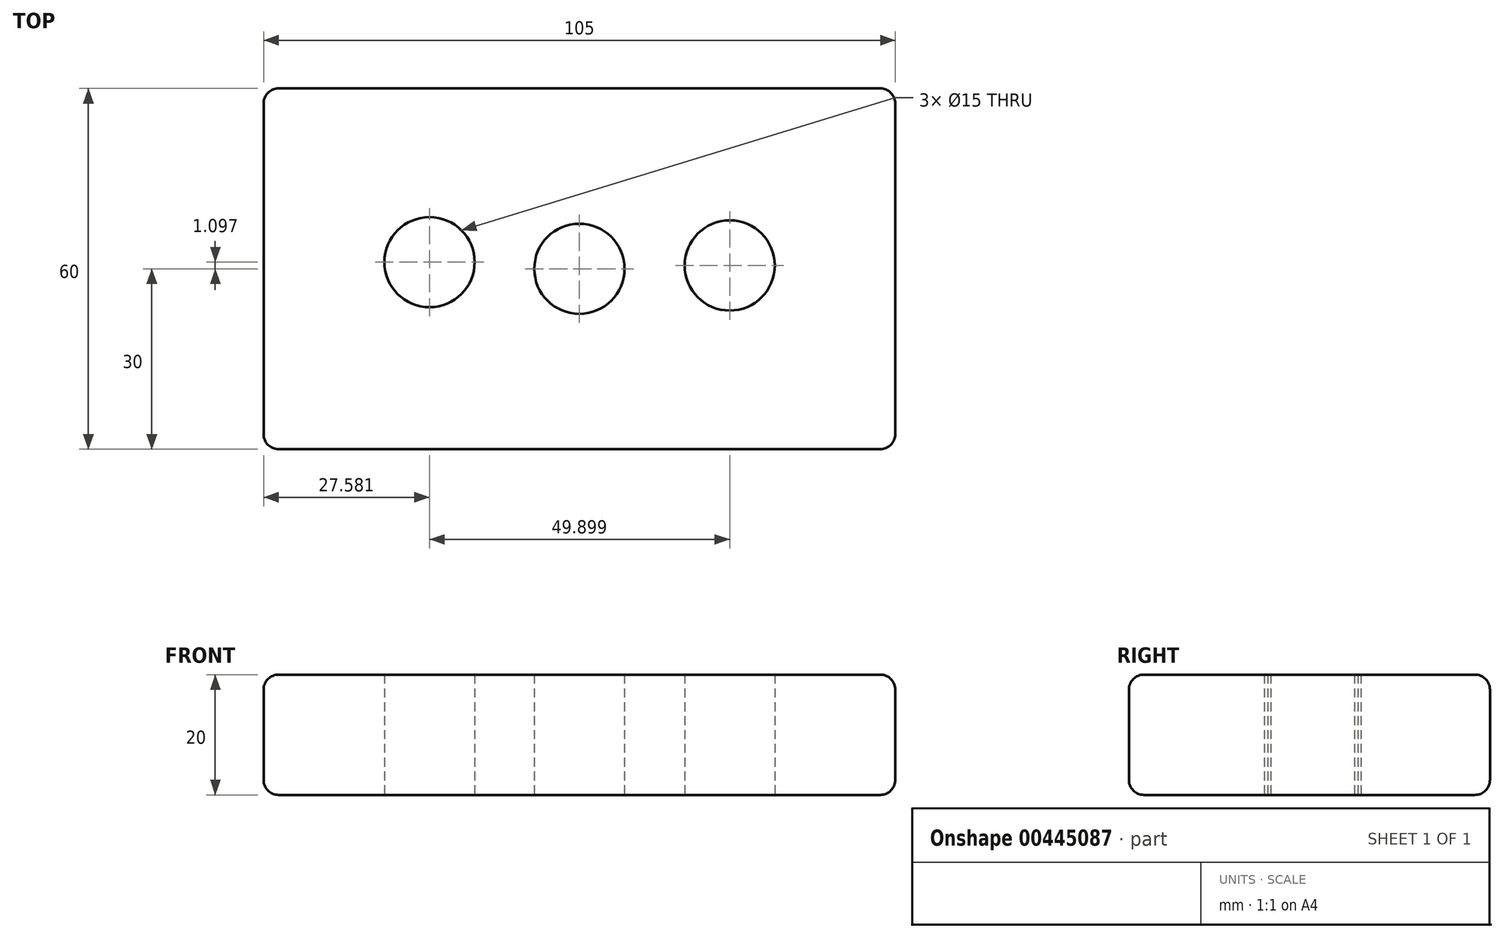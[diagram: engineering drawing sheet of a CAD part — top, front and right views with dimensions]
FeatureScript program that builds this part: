
annotation { "Feature Type Name" : "Feature", "Feature Type Description" : "" }
export const myFeature = defineFeature(function(context is Context, id is Id, definition is map)
    precondition{}
    {
        {
            var Q0;
            Q0=qCreatedBy(makeId("Top.planeOp"),FACE);
            var sketch = newSketch(context, id + "F0", { "sketchPlane" : qUnion([Q0])});
            skLineSegment(sketch, "E0.bottom", {"start": v(52.5, 30) * mm, "end": v(-52.5, 30) * mm});
            skLineSegment(sketch, "E0.top", {"start": v(52.5, -30) * mm, "end": v(-52.5, -30) * mm});
            skLineSegment(sketch, "E0.left", {"start": v(52.5, 30) * mm, "end": v(52.5, -30) * mm});
            skLineSegment(sketch, "E0.right", {"start": v(-52.5, 30) * mm, "end": v(-52.5, -30) * mm});
            skPoint(sketch, "E0.middle", {"position": v(0, 0) * mm});
            skCircle(sketch, "E1", {"center": v(0, 0) * mm, "radius": 7.5 * mm});
            skLineSegment(sketch, "E2", {"start": v(7.5, 0) * mm, "end": v(17.5, 0) * mm});
            skLineSegment(sketch, "E3", {"start": v(-7.5, 0) * mm, "end": v(-17.5, 0) * mm});
            skCircle(sketch, "E4", {"center": v(24.98, 0.55) * mm, "radius": 7.5 * mm});
            skPoint(sketch, "E4.second.point", {"position": v(31.94, 3.34) * mm});
            skPoint(sketch, "E4.third.point", {"position": v(31.73, -2.72) * mm});
            skCircle(sketch, "E5", {"center": v(-24.92, 1.1) * mm, "radius": 7.5 * mm});
            skPoint(sketch, "E5.second.point", {"position": v(-32.03, 3.48) * mm});
            skPoint(sketch, "E5.third.point", {"position": v(-25.9, -6.34) * mm});
            skSolve(sketch);
        }
        {
            var Q0;
            Q0=makeQuery(id+"F0.imprint","IMPRINT",FACE,{"disambiguationData":[TD([[makeQuery(id+"F0.imprint","IMPRINT",EDGE,{"derivedFrom":sQuery(id+"F0.wireOp",EDGE,"E0.bottom")}),1.0]])]});
            extrude(context, id + "F1", {"entities" : qUnion([Q0]), "depth" : 20 * mm});
        }
        {
            var Q0;
            Q0=makeQuery(id+"F1.opExtrude","CAP_EDGE",EDGE,{"disambiguationData":[OSD([sQuery(id+"F0.wireOp",EDGE,"E0.top")])],"isStart":false});
            fillet(context, id + "F2", {"entities" : qUnion([Q0]), "radius" : 2.5 * mm, "tangentPropagation" : true, "allowEdgeOverflow" : false});
        }
        {
            var Q0;
            Q0=makeQuery(id+"F1.opExtrude","CAP_EDGE",EDGE,{"disambiguationData":[OSD([sQuery(id+"F0.wireOp",EDGE,"E0.left")])],"isStart":false});
            var Q1;
            Q1=makeQuery(id+"F1.opExtrude","CAP_EDGE",EDGE,{"disambiguationData":[OSD([sQuery(id+"F0.wireOp",EDGE,"E0.bottom")])],"isStart":false});
            fillet(context, id + "F3", {"entities" : qUnion([Q0, Q1]), "radius" : 2.5 * mm, "tangentPropagation" : true, "allowEdgeOverflow" : false});
        }
        {
            var Q0;
            Q0=makeQuery(id+"F1.opExtrude","CAP_EDGE",EDGE,{"disambiguationData":[OSD([sQuery(id+"F0.wireOp",EDGE,"E0.right")])],"isStart":false});
            fillet(context, id + "F4", {"entities" : qUnion([Q0]), "radius" : 2.5 * mm, "tangentPropagation" : true, "allowEdgeOverflow" : false});
        }
        {
            var Q0;
            Q0=makeQuery(id+"F1.opExtrude","SWEPT_EDGE",EDGE,{"disambiguationData":[OSD([sQuery(id+"F0.wireOp",EDGE,"E0.bottom"),sQuery(id+"F0.wireOp",EDGE,"E0.left")])]});
            fillet(context, id + "F5", {"entities" : qUnion([Q0]), "radius" : 2.5 * mm, "tangentPropagation" : true, "allowEdgeOverflow" : false});
        }
        {
            var Q0;
            Q0=makeQuery(id+"F1.opExtrude","CAP_EDGE",EDGE,{"disambiguationData":[OSD([sQuery(id+"F0.wireOp",EDGE,"E0.left")])],"isStart":true});
            fillet(context, id + "F6", {"entities" : qUnion([Q0]), "radius" : 2.5 * mm, "tangentPropagation" : true, "allowEdgeOverflow" : false});
        }
    });
